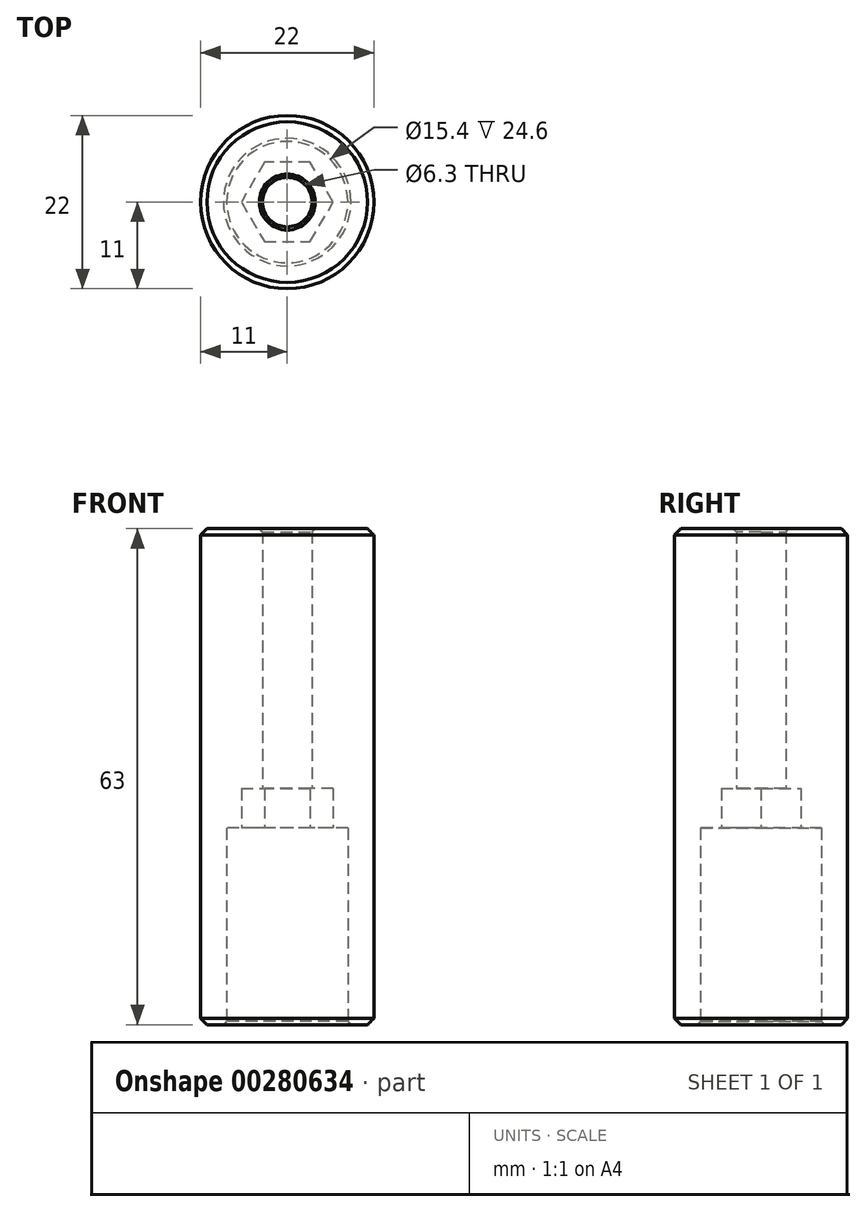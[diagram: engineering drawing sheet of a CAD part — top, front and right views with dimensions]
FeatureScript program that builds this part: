
annotation { "Feature Type Name" : "Feature", "Feature Type Description" : "" }
export const myFeature = defineFeature(function(context is Context, id is Id, definition is map)
    precondition{}
    {
        {
            var Q0;
            Q0=qCreatedBy(makeId("Top.planeOp"),FACE);
            var sketch = newSketch(context, id + "F0", { "sketchPlane" : qUnion([Q0])});
            skCircle(sketch, "E0", {"center": v(0, 0) * mm, "radius": 11 * mm});
            skCircle(sketch, "E1", {"center": v(0, 0) * mm, "radius": 7.7 * mm});
            skSolve(sketch);
        }
        {
            var Q0;
            Q0=qSketchRegion(id+"F0",true);
            extrude(context, id + "F1", {"entities" : qUnion([Q0]), "depth" : 25 * mm});
        }
        {
            var Q0;
            Q0=makeQuery(id+"F1.opExtrude","CAP_FACE",FACE,{"disambiguationData":[OSD([sQuery(id+"F0.wireOp",EDGE,"E0"),sQuery(id+"F0.wireOp",EDGE,"E1")])],"isStart":false});
            var sketch = newSketch(context, id + "F2", { "sketchPlane" : qUnion([Q0])});
            skCircle(sketch, "E2.0", {"center": v(0, 0) * mm, "radius": 11 * mm});
            skSolve(sketch);
        }
        {
            var Q0;
            Q0=qSketchRegion(id+"F2",true);
            extrude(context, id + "F3", {"entities" : qUnion([Q0]), "operationType" : NewBodyOperationType.ADD, "depth" : 38 * mm});
        }
        {
            var Q0;
            Q0=makeQuery(id+"F3.opExtrude","CAP_FACE",FACE,{"disambiguationData":[OSD([sQuery(id+"F2.wireOp",EDGE,"E2.0")])],"isStart":true});
            var sketch = newSketch(context, id + "F4", { "sketchPlane" : qUnion([Q0])});
            skCircle(sketch, "E3.cCircle", {"center": v(0, 0) * mm, "radius": 5.05 * mm, "construction": true});
            skLineSegment(sketch, "E3.0", {"start": v(2.92, -5.05) * mm, "end": v(-2.92, -5.05) * mm});
            skLineSegment(sketch, "E3.1", {"start": v(-2.92, -5.05) * mm, "end": v(-5.83, 0) * mm});
            skLineSegment(sketch, "E3.2", {"start": v(-5.83, 0) * mm, "end": v(-2.92, 5.05) * mm});
            skLineSegment(sketch, "E3.3", {"start": v(-2.92, 5.05) * mm, "end": v(2.92, 5.05) * mm});
            skLineSegment(sketch, "E3.4", {"start": v(2.92, 5.05) * mm, "end": v(5.83, 0) * mm});
            skLineSegment(sketch, "E3.5", {"start": v(5.83, 0) * mm, "end": v(2.92, -5.05) * mm});
            skPoint(sketch, "E3.0.midPoint", {"position": v(0, -5.05) * mm});
            skSolve(sketch);
        }
        {
            var Q0;
            Q0=qSketchRegion(id+"F4",true);
            extrude(context, id + "F5", {"entities" : qUnion([Q0]), "operationType" : NewBodyOperationType.REMOVE, "oppositeDirection" : true, "depth" : 5 * mm});
        }
        {
            var Q0;
            Q0=makeQuery(id+"F5.boolean.opBoolean","COPY",FACE,{"derivedFrom":makeQuery(id+"F5.opExtrude","CAP_FACE",FACE,{"disambiguationData":[OSD([sQuery(id+"F4.wireOp",EDGE,"E3.0"),sQuery(id+"F4.wireOp",EDGE,"E3.1"),sQuery(id+"F4.wireOp",EDGE,"E3.2"),sQuery(id+"F4.wireOp",EDGE,"E3.3"),sQuery(id+"F4.wireOp",EDGE,"E3.4"),sQuery(id+"F4.wireOp",EDGE,"E3.5")])],"isStart":false})});
            var sketch = newSketch(context, id + "F6", { "sketchPlane" : qUnion([Q0])});
            skCircle(sketch, "E4", {"center": v(0, 0) * mm, "radius": 3.15 * mm});
            skSolve(sketch);
        }
        {
            var Q0;
            Q0=qSketchRegion(id+"F6",true);
            extrude(context, id + "F7", {"entities" : qUnion([Q0]), "operationType" : NewBodyOperationType.REMOVE, "oppositeDirection" : true, "depth" : 50 * mm});
        }
        {
            var Q0;
            Q0=makeQuery(id+"F1.opExtrude","CAP_EDGE",EDGE,{"disambiguationData":[OSD([sQuery(id+"F0.wireOp",EDGE,"E0")])],"isStart":true});
            var Q1;
            Q1=makeQuery(id+"F3.opExtrude","CAP_EDGE",EDGE,{"disambiguationData":[OSD([sQuery(id+"F2.wireOp",EDGE,"E2.0")])],"isStart":false});
            chamfer(context, id + "F8", {"entities" : qUnion([Q0, Q1]), "width" : 0.8 * mm, "tangentPropagation" : true});
        }
        {
            var Q0;
            Q0=makeQuery(id+"F7.boolean.opBoolean","INTERSECT",EDGE,{"derivedFrom":[makeQuery(id+"F3.opExtrude","CAP_FACE",FACE,{"disambiguationData":[OSD([sQuery(id+"F2.wireOp",EDGE,"E2.0")])],"isStart":false}),makeQuery(id+"F7.opExtrude","SWEPT_FACE",FACE,{"disambiguationData":[OSD([sQuery(id+"F6.wireOp",EDGE,"E4")])]})]});
            chamfer(context, id + "F9", {"entities" : qUnion([Q0]), "width" : 0.4 * mm, "tangentPropagation" : true});
        }
        {
            var Q0;
            Q0=makeQuery(id+"F1.opExtrude","CAP_EDGE",EDGE,{"disambiguationData":[OSD([sQuery(id+"F0.wireOp",EDGE,"E1")])],"isStart":true});
            chamfer(context, id + "F10", {"entities" : qUnion([Q0]), "width" : 0.4 * mm, "tangentPropagation" : true});
        }
    });
